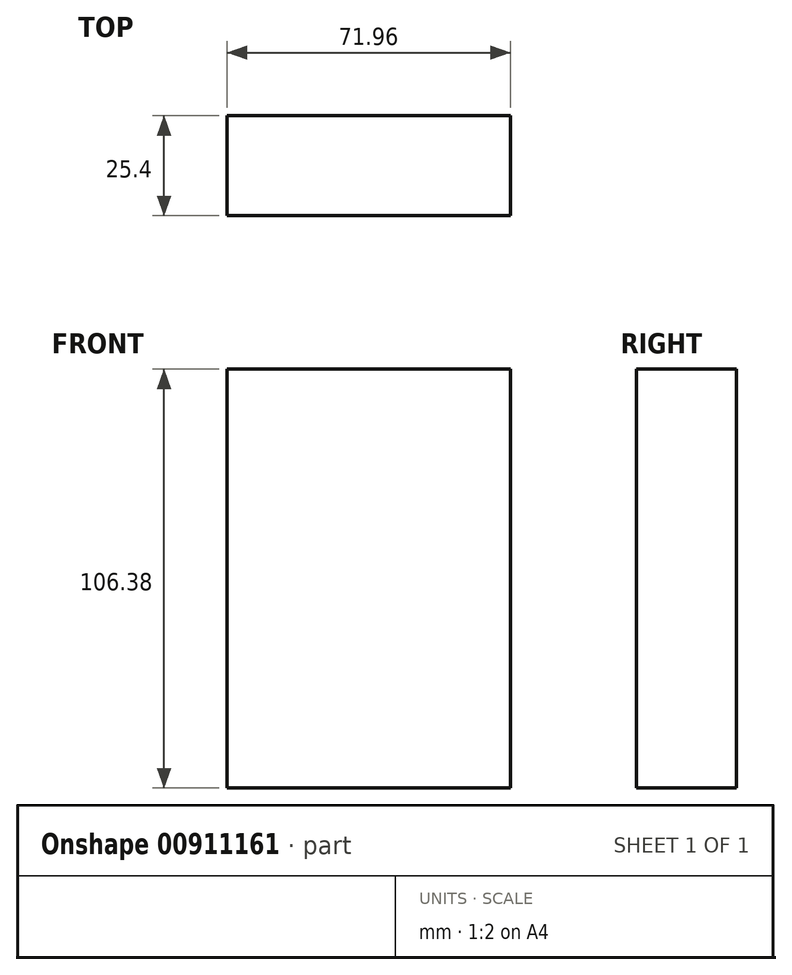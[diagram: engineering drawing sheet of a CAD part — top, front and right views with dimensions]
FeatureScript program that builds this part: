
annotation { "Feature Type Name" : "Feature", "Feature Type Description" : "" }
export const myFeature = defineFeature(function(context is Context, id is Id, definition is map)
    precondition{}
    {
        {
            var Q0;
            Q0=qCreatedBy(makeId("Front.planeOp"),FACE);
            var sketch = newSketch(context, id + "F0", { "sketchPlane" : qUnion([Q0])});
            skLineSegment(sketch, "E0.bottom", {"start": v(-35.84, 0) * mm, "end": v(36.12, 0) * mm});
            skLineSegment(sketch, "E0.top", {"start": v(-35.84, 106.38) * mm, "end": v(36.12, 106.38) * mm});
            skLineSegment(sketch, "E0.left", {"start": v(-35.84, 0) * mm, "end": v(-35.84, 106.38) * mm});
            skLineSegment(sketch, "E0.right", {"start": v(36.12, 0) * mm, "end": v(36.12, 106.38) * mm});
            skSolve(sketch);
        }
        {
            var Q0;
            Q0 = qSketchRegion(id + "F0", true);
            extrude(context, id + "F1", {"entities" : qUnion([Q0]), "depth" : 25.4 * mm, "offsetDistance" : 25.4 * mm});
        }
    });
